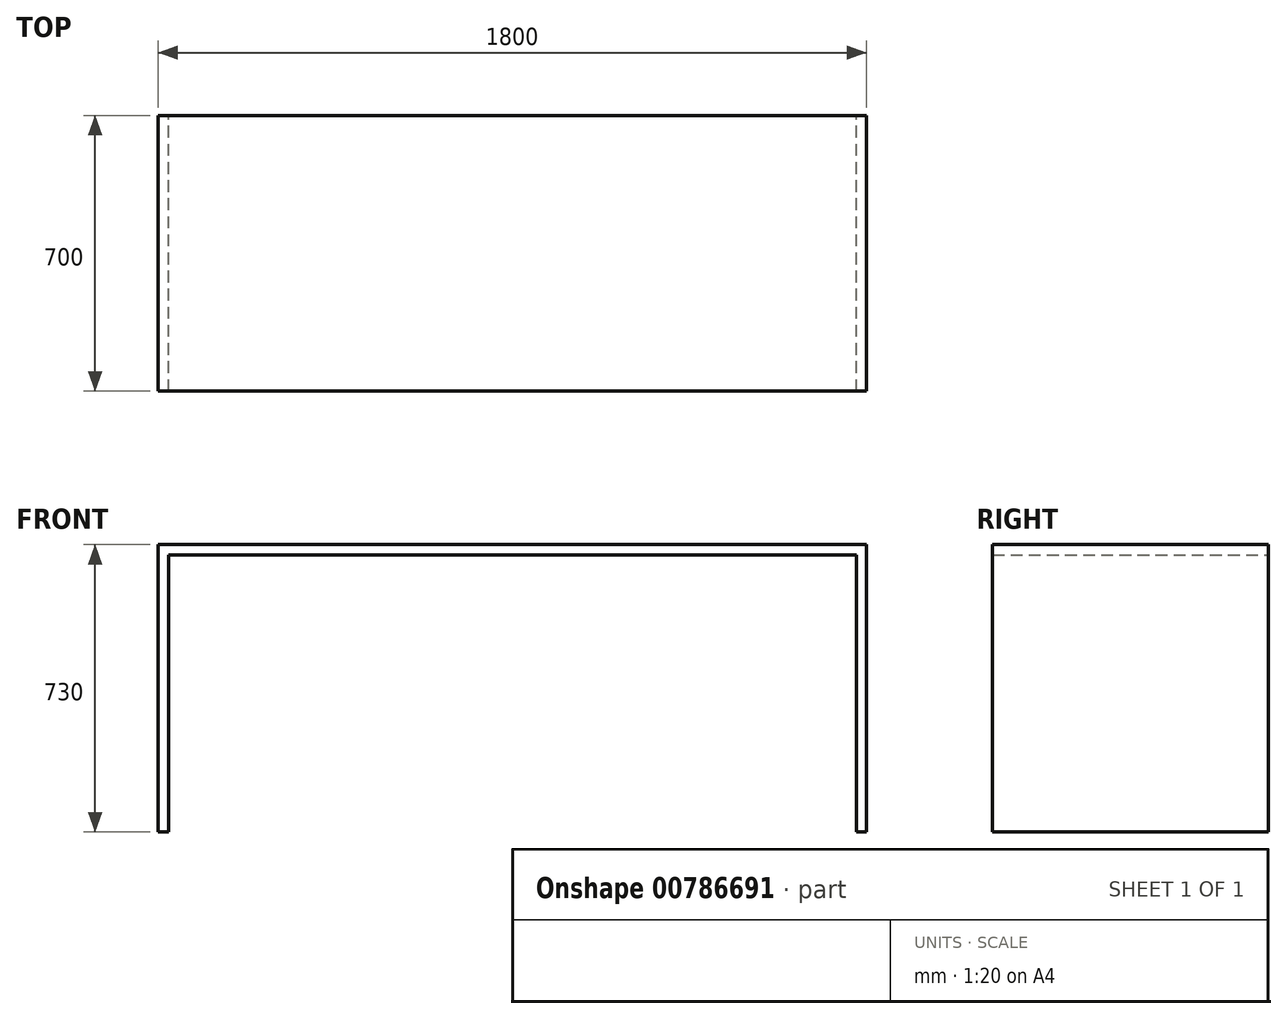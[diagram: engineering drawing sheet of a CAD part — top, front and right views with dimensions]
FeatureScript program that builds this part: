
annotation { "Feature Type Name" : "Feature", "Feature Type Description" : "" }
export const myFeature = defineFeature(function(context is Context, id is Id, definition is map)
    precondition{}
    {
        {
            var Q0;
            Q0=qCreatedBy(makeId("Front.planeOp"),FACE);
            var sketch = newSketch(context, id + "F0", { "sketchPlane" : qUnion([Q0])});
            skLineSegment(sketch, "E0", {"start": v(0, 0) * mm, "end": v(0, 730) * mm});
            skLineSegment(sketch, "E1", {"start": v(0, 730) * mm, "end": v(1800, 730) * mm});
            skLineSegment(sketch, "E2", {"start": v(1800, 730) * mm, "end": v(1800, 0) * mm});
            skLineSegment(sketch, "E3", {"start": v(0, 0) * mm, "end": v(26, 0) * mm});
            skLineSegment(sketch, "E4", {"start": v(26, 0) * mm, "end": v(26, 704) * mm});
            skLineSegment(sketch, "E5", {"start": v(26, 704) * mm, "end": v(1774, 704) * mm});
            skLineSegment(sketch, "E6", {"start": v(1774, 704) * mm, "end": v(1774, 0) * mm});
            skLineSegment(sketch, "E7", {"start": v(1774, 0) * mm, "end": v(1800, 0) * mm});
            skSolve(sketch);
        }
        {
            var Q0;
            Q0=makeQuery(id+"F0.imprint","IMPRINT",FACE,{"disambiguationData":[TD([[makeQuery(id+"F0.imprint","IMPRINT",EDGE,{"derivedFrom":sQuery(id+"F0.wireOp",EDGE,"E0")}),-1.0]])]});
            extrude(context, id + "F1", {"entities" : qUnion([Q0]), "depth" : 700 * mm, "offsetDistance" : 25 * mm});
        }
    });
